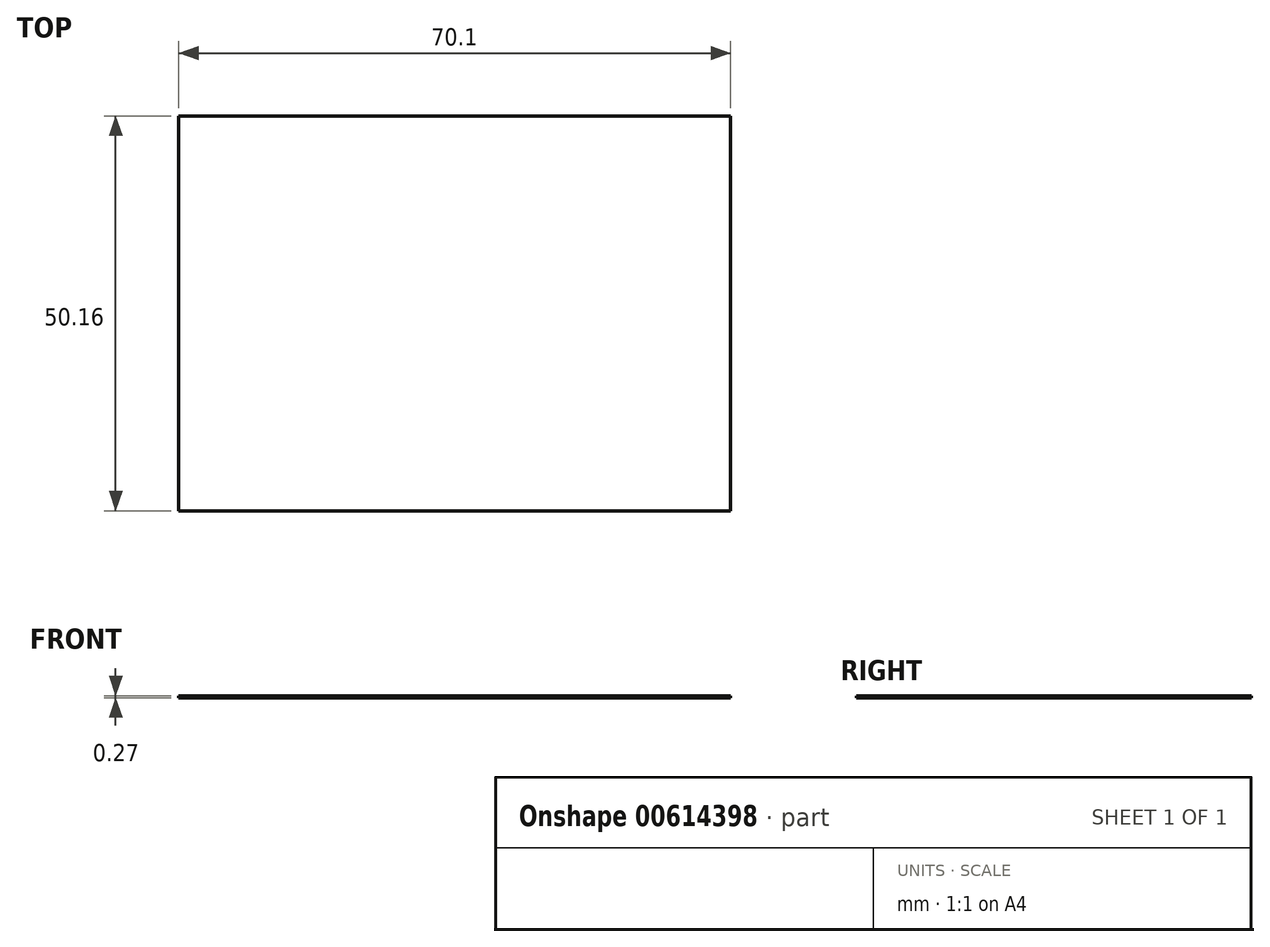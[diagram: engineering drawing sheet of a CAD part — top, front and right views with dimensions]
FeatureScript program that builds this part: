
annotation { "Feature Type Name" : "Feature", "Feature Type Description" : "" }
export const myFeature = defineFeature(function(context is Context, id is Id, definition is map)
    precondition{}
    {
        {
            var Q0;
            Q0=qCreatedBy(makeId("Top.planeOp"),FACE);
            var sketch = newSketch(context, id + "F0", { "sketchPlane" : qUnion([Q0])});
            skLineSegment(sketch, "E0.bottom", {"start": v(35.05, -25.08) * mm, "end": v(-35.05, -25.08) * mm});
            skLineSegment(sketch, "E0.top", {"start": v(35.05, 25.08) * mm, "end": v(-35.05, 25.08) * mm});
            skLineSegment(sketch, "E0.left", {"start": v(35.05, -25.08) * mm, "end": v(35.05, 25.08) * mm});
            skLineSegment(sketch, "E0.right", {"start": v(-35.05, -25.08) * mm, "end": v(-35.05, 25.08) * mm});
            skPoint(sketch, "E0.middle", {"position": v(0, 0) * mm});
            skSolve(sketch);
        }
        {
            var Q0;
            Q0 = qSketchRegion(id + "F0", true);
            extrude(context, id + "F1", {"entities" : qUnion([Q0]), "depth" : 0.27 * mm, "offsetDistance" : 25.4 * mm});
        }
    });
